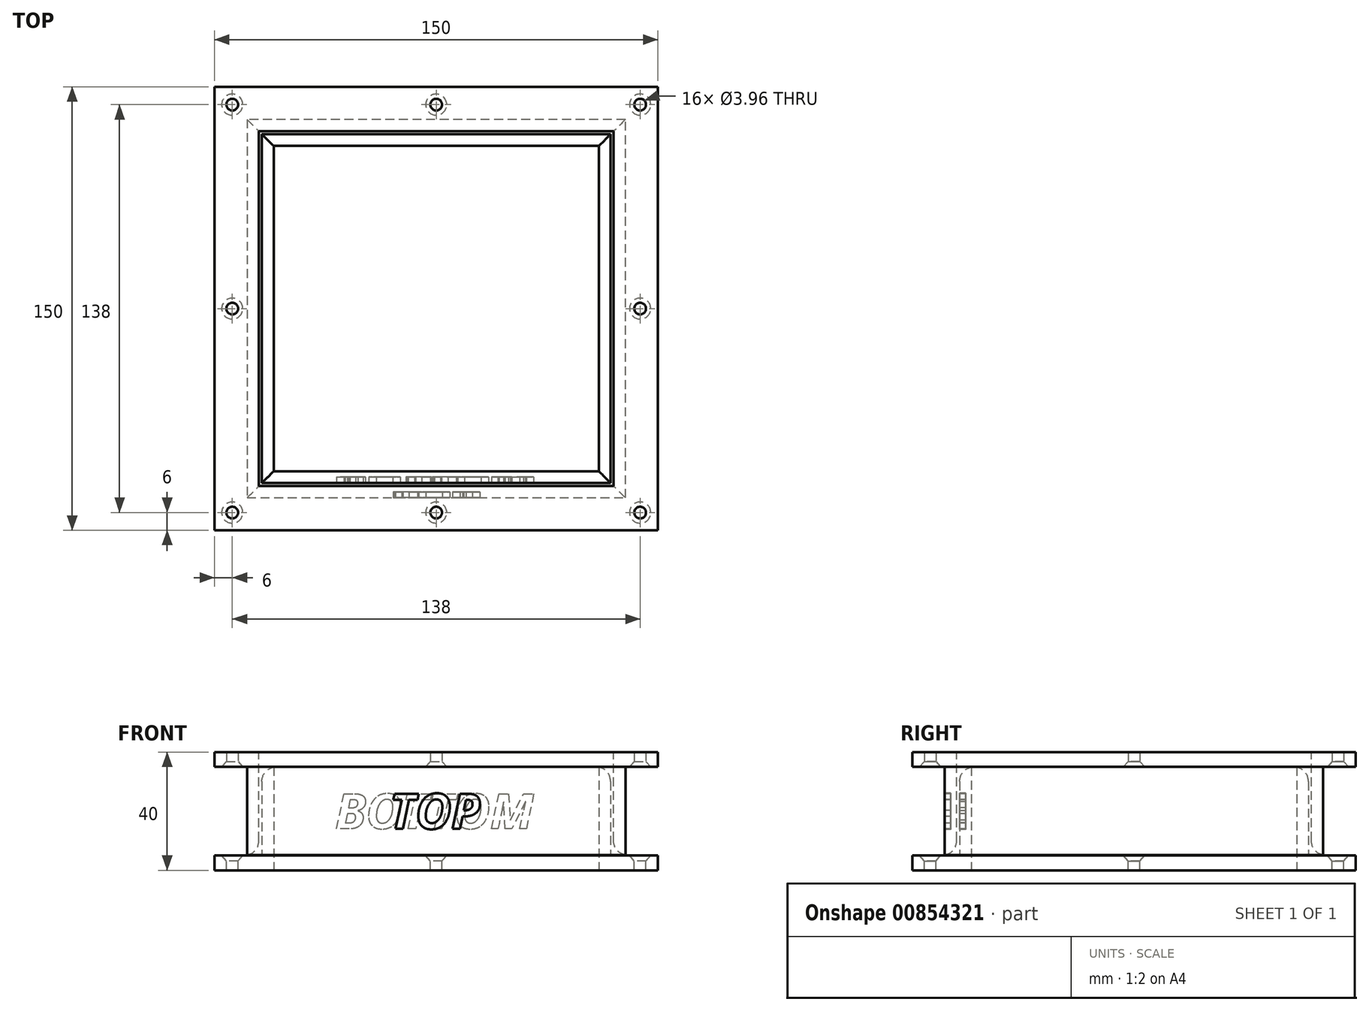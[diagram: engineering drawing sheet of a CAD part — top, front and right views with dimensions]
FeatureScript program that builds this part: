
annotation { "Feature Type Name" : "Feature", "Feature Type Description" : "" }
export const myFeature = defineFeature(function(context is Context, id is Id, definition is map)
    precondition{}
    {
        {
            var Q0;
            Q0=qCreatedBy(makeId("Top.planeOp"),FACE);
            var sketch = newSketch(context, id + "F0", { "sketchPlane" : qUnion([Q0])});
            skLineSegment(sketch, "E0.bottom", {"start": v(-75, 75) * mm, "end": v(75, 75) * mm});
            skLineSegment(sketch, "E0.top", {"start": v(-75, -75) * mm, "end": v(75, -75) * mm});
            skLineSegment(sketch, "E0.left", {"start": v(-75, 75) * mm, "end": v(-75, -75) * mm});
            skLineSegment(sketch, "E0.right", {"start": v(75, 75) * mm, "end": v(75, -75) * mm});
            skLineSegment(sketch, "E1.bottom", {"start": v(-55, 55) * mm, "end": v(55, 55) * mm});
            skLineSegment(sketch, "E1.top", {"start": v(-55, -55) * mm, "end": v(55, -55) * mm});
            skLineSegment(sketch, "E1.left", {"start": v(-55, 55) * mm, "end": v(-55, -55) * mm});
            skLineSegment(sketch, "E1.right", {"start": v(55, 55) * mm, "end": v(55, -55) * mm});
            skLineSegment(sketch, "E2", {"start": v(0, -75) * mm, "end": v(0, 75) * mm, "construction": true});
            skLineSegment(sketch, "E3", {"start": v(-75, 0) * mm, "end": v(75, 0) * mm, "construction": true});
            skSolve(sketch);
        }
        {
            var Q0;
            Q0 = qSketchRegion(id + "F0", true);
            extrude(context, id + "F1", {"entities" : qUnion([Q0]), "depth" : 5 * mm, "offsetDistance" : 25 * mm});
        }
        {
            var Q0;
            Q0=makeQuery(id+"F1.opExtrude","CAP_FACE",FACE,{"disambiguationData":[OSD([sQuery(id+"F0.wireOp",EDGE,"E0.bottom"),sQuery(id+"F0.wireOp",EDGE,"E0.top"),sQuery(id+"F0.wireOp",EDGE,"E0.left"),sQuery(id+"F0.wireOp",EDGE,"E0.right"),sQuery(id+"F0.wireOp",EDGE,"E1.bottom"),sQuery(id+"F0.wireOp",EDGE,"E1.top"),sQuery(id+"F0.wireOp",EDGE,"E1.left"),sQuery(id+"F0.wireOp",EDGE,"E1.right")])],"isStart":false});
            var sketch = newSketch(context, id + "F2", { "sketchPlane" : qUnion([Q0])});
            skLineSegment(sketch, "E4.0", {"start": v(-55, 55) * mm, "end": v(55, 55) * mm});
            skLineSegment(sketch, "E4.1", {"start": v(-55, 55) * mm, "end": v(-55, -55) * mm});
            skLineSegment(sketch, "E5.0", {"start": v(-55, -55) * mm, "end": v(55, -55) * mm});
            skLineSegment(sketch, "E5.1", {"start": v(55, 55) * mm, "end": v(55, -55) * mm});
            skLineSegment(sketch, "E6.bottom", {"start": v(-59, 59) * mm, "end": v(59, 59) * mm});
            skLineSegment(sketch, "E6.top", {"start": v(-59, -59) * mm, "end": v(59, -59) * mm});
            skLineSegment(sketch, "E6.left", {"start": v(-59, 59) * mm, "end": v(-59, -59) * mm});
            skLineSegment(sketch, "E6.right", {"start": v(59, 59) * mm, "end": v(59, -59) * mm});
            skLineSegment(sketch, "E7", {"start": v(0, -48) * mm, "end": v(0, 49.58) * mm, "construction": true});
            skLineSegment(sketch, "E8", {"start": v(-49.37, 0) * mm, "end": v(50.06, 0) * mm, "construction": true});
            skSolve(sketch);
        }
        {
            var Q0;
            Q0 = qSketchRegion(id + "F2", true);
            extrude(context, id + "F3", {"entities" : qUnion([Q0]), "operationType" : NewBodyOperationType.ADD, "depth" : 30 * mm, "offsetDistance" : 25 * mm});
        }
        {
            var Q0;
            Q0=makeQuery(id+"F3.opExtrude","CAP_FACE",FACE,{"disambiguationData":[OSD([sQuery(id+"F2.wireOp",EDGE,"E4.0"),sQuery(id+"F2.wireOp",EDGE,"E4.1"),sQuery(id+"F2.wireOp",EDGE,"E5.0"),sQuery(id+"F2.wireOp",EDGE,"E5.1"),sQuery(id+"F2.wireOp",EDGE,"E6.bottom"),sQuery(id+"F2.wireOp",EDGE,"E6.top"),sQuery(id+"F2.wireOp",EDGE,"E6.left"),sQuery(id+"F2.wireOp",EDGE,"E6.right")])],"isStart":false});
            var sketch = newSketch(context, id + "F4", { "sketchPlane" : qUnion([Q0])});
            skLineSegment(sketch, "E9.0", {"start": v(-59, 59) * mm, "end": v(59, 59) * mm, "construction": true});
            skLineSegment(sketch, "E9.1", {"start": v(-59, 59) * mm, "end": v(-59, -59) * mm, "construction": true});
            skLineSegment(sketch, "E9.2", {"start": v(-59, -59) * mm, "end": v(59, -59) * mm, "construction": true});
            skLineSegment(sketch, "E9.3", {"start": v(59, 59) * mm, "end": v(59, -59) * mm, "construction": true});
            skLineSegment(sketch, "E10.0", {"start": v(-64, 64) * mm, "end": v(64, 64) * mm});
            skLineSegment(sketch, "E10.1", {"start": v(-64, 64) * mm, "end": v(-64, -64) * mm});
            skLineSegment(sketch, "E10.2", {"start": v(-64, -64) * mm, "end": v(64, -64) * mm});
            skLineSegment(sketch, "E10.3", {"start": v(64, 64) * mm, "end": v(64, -64) * mm});
            skLineSegment(sketch, "E11.0", {"start": v(-60, -60) * mm, "end": v(60, -60) * mm});
            skLineSegment(sketch, "E11.1", {"start": v(-60, 60) * mm, "end": v(-60, -60) * mm});
            skLineSegment(sketch, "E11.2", {"start": v(-60, 60) * mm, "end": v(60, 60) * mm});
            skLineSegment(sketch, "E11.3", {"start": v(60, 60) * mm, "end": v(60, -60) * mm});
            skSolve(sketch);
        }
        {
            var Q0;
            Q0 = qSketchRegion(id + "F4", true);
            extrude(context, id + "F5", {"entities" : qUnion([Q0]), "oppositeDirection" : true, "depth" : 30 * mm, "offsetDistance" : 25 * mm});
        }
        {
            var Q0;
            Q0=makeQuery(id+"F5.opExtrude","CAP_FACE",FACE,{"disambiguationData":[OSD([sQuery(id+"F4.wireOp",EDGE,"E9.0"),sQuery(id+"F4.wireOp",EDGE,"E9.1"),sQuery(id+"F4.wireOp",EDGE,"E9.2"),sQuery(id+"F4.wireOp",EDGE,"E9.3"),sQuery(id+"F4.wireOp",EDGE,"E10.0"),sQuery(id+"F4.wireOp",EDGE,"E10.1"),sQuery(id+"F4.wireOp",EDGE,"E10.2"),sQuery(id+"F4.wireOp",EDGE,"E10.3")])],"isStart":true});
            var sketch = newSketch(context, id + "F6", { "sketchPlane" : qUnion([Q0])});
            skLineSegment(sketch, "E12.0", {"start": v(75, 75) * mm, "end": v(75, -75) * mm});
            skLineSegment(sketch, "E12.1", {"start": v(-75, 75) * mm, "end": v(75, 75) * mm});
            skLineSegment(sketch, "E12.2", {"start": v(-75, 75) * mm, "end": v(-75, -75) * mm});
            skLineSegment(sketch, "E12.3", {"start": v(-75, -75) * mm, "end": v(75, -75) * mm});
            skLineSegment(sketch, "E13.0", {"start": v(-60, -60) * mm, "end": v(60, -60) * mm});
            skLineSegment(sketch, "E13.1", {"start": v(-60, 60) * mm, "end": v(-60, -60) * mm});
            skLineSegment(sketch, "E13.2", {"start": v(-60, 60) * mm, "end": v(60, 60) * mm});
            skLineSegment(sketch, "E13.3", {"start": v(60, 60) * mm, "end": v(60, -60) * mm});
            skSolve(sketch);
        }
        {
            var Q0;
            Q0 = qSketchRegion(id + "F6", true);
            extrude(context, id + "F7", {"entities" : qUnion([Q0]), "operationType" : NewBodyOperationType.ADD, "depth" : 5 * mm, "offsetDistance" : 25 * mm});
        }
        {
            var Q0;
            Q0=makeQuery(id+"F1.opExtrude","CAP_FACE",FACE,{"disambiguationData":[OSD([sQuery(id+"F0.wireOp",EDGE,"E0.bottom"),sQuery(id+"F0.wireOp",EDGE,"E0.top"),sQuery(id+"F0.wireOp",EDGE,"E0.left"),sQuery(id+"F0.wireOp",EDGE,"E0.right"),sQuery(id+"F0.wireOp",EDGE,"E1.bottom"),sQuery(id+"F0.wireOp",EDGE,"E1.top"),sQuery(id+"F0.wireOp",EDGE,"E1.left"),sQuery(id+"F0.wireOp",EDGE,"E1.right")])],"isStart":false});
            var sketch = newSketch(context, id + "F8", { "sketchPlane" : qUnion([Q0])});
            skPoint(sketch, "E14", {"position": v(-69, 69) * mm});
            skPoint(sketch, "E15", {"position": v(69, 69) * mm});
            skPoint(sketch, "E16", {"position": v(-69, -69) * mm});
            skPoint(sketch, "E17", {"position": v(69, -69) * mm});
            skPoint(sketch, "E18", {"position": v(0, 69) * mm});
            skPoint(sketch, "E19", {"position": v(-69, 0) * mm});
            skPoint(sketch, "E20", {"position": v(0, -69) * mm});
            skPoint(sketch, "E21", {"position": v(69, 0) * mm});
            skSolve(sketch);
        }
        {
            var Q0;
            Q0=sQuery(id+"F8.wireOp",VERTEX,"E14");
            var Q1;
            Q1=sQuery(id+"F8.wireOp",VERTEX,"E15");
            var Q2;
            Q2=sQuery(id+"F8.wireOp",VERTEX,"E17");
            var Q3;
            Q3=sQuery(id+"F8.wireOp",VERTEX,"E16");
            var Q4;
            Q4=sQuery(id+"F8.wireOp",VERTEX,"E19");
            var Q5;
            Q5=sQuery(id+"F8.wireOp",VERTEX,"E18");
            var Q6;
            Q6=sQuery(id+"F8.wireOp",VERTEX,"E20");
            var Q7;
            Q7=sQuery(id+"F8.wireOp",VERTEX,"E21");
            var Q8;
            Q8=makeQuery(id+"F1.opExtrude","SWEPT_BODY",BODY,{"disambiguationData":[OSD([sQuery(id+"F0.wireOp",EDGE,"E0.bottom"),sQuery(id+"F0.wireOp",EDGE,"E0.top"),sQuery(id+"F0.wireOp",EDGE,"E0.left"),sQuery(id+"F0.wireOp",EDGE,"E0.right"),sQuery(id+"F0.wireOp",EDGE,"E1.bottom"),sQuery(id+"F0.wireOp",EDGE,"E1.top"),sQuery(id+"F0.wireOp",EDGE,"E1.left"),sQuery(id+"F0.wireOp",EDGE,"E1.right")])]});
            hole(context, id + "F9", {"style" : HoleStyle.C_SINK, "endStyle" : HoleEndStyle.THROUGH, "standardTappedOrClearance" : lookupTablePath({ "fit" : "Normal (ASME)", "standard" : "ANSI", "size" : "#5", "type" : "Clearance" }), "standardBlindInLast" : lookupTablePath({ "fit" : "Normal", "standard" : "ANSI", "engagement" : "75%", "pitch" : "40 tpi", "size" : "#5", "type" : "Clearance & tapped" }), "holeDiameter" : 3.96 * mm, "cSinkDiameter" : 7.14 * mm, "cSinkAngle" : 82 * degree, "majorDiameter" : 3.5 * mm, "isTappedThrough" : true, "tappedDepth" : 12 * mm, "tapClearance" : 3, "locations" : qUnion([Q0, Q1, Q2, Q3, Q4, Q5, Q6, Q7]), "scope" : qUnion([Q8])});
        }
        {
            var Q0;
            Q0=makeQuery(id+"F3.opExtrude","SWEPT_FACE",FACE,{"disambiguationData":[OSD([sQuery(id+"F2.wireOp",EDGE,"E6.top")])]});
            var sketch = newSketch(context, id + "F10", { "sketchPlane" : qUnion([Q0])});
            skLineSegment(sketch, "E22", {"start": v(-59, 20) * mm, "end": v(59, 20) * mm, "construction": true});
            skLineSegment(sketch, "E23", {"start": v(0, 35) * mm, "end": v(0, 5) * mm, "construction": true});
            skText(sketch, "E24", { "text": "BOTTOM", "fontName": "OpenSans-BoldItalic.ttf"});
            const initialGuessF10  = {"E24": [-0.0341, 0.014, 1, 0, 0.012]};
            skSetInitialGuess(sketch, initialGuessF10);
            skSolve(sketch);
        }
        {
            var Q0;
            Q0 = qSketchRegion(id + "F10", true);
            extrude(context, id + "F11", {"entities" : qUnion([Q0]), "operationType" : NewBodyOperationType.REMOVE, "oppositeDirection" : true, "depth" : 2 * mm, "offsetDistance" : 25 * mm});
        }
        {
            var Q0;
            Q0=makeQuery(id+"F7.opExtrude","CAP_FACE",FACE,{"disambiguationData":[OSD([sQuery(id+"F6.wireOp",EDGE,"E12.0"),sQuery(id+"F6.wireOp",EDGE,"E12.1"),sQuery(id+"F6.wireOp",EDGE,"E12.2"),sQuery(id+"F6.wireOp",EDGE,"E12.3"),sQuery(id+"F6.wireOp",EDGE,"147194ed-eec6-48fc-bbfb-cd27aaa17bc2.0"),sQuery(id+"F6.wireOp",EDGE,"147194ed-eec6-48fc-bbfb-cd27aaa17bc2.1"),sQuery(id+"F6.wireOp",EDGE,"147194ed-eec6-48fc-bbfb-cd27aaa17bc2.2"),sQuery(id+"F6.wireOp",EDGE,"147194ed-eec6-48fc-bbfb-cd27aaa17bc2.3")])],"isStart":true});
            var sketch = newSketch(context, id + "F12", { "sketchPlane" : qUnion([Q0])});
            skPoint(sketch, "E25", {"position": v(-69, 69) * mm});
            skPoint(sketch, "E26", {"position": v(-69, -69) * mm});
            skPoint(sketch, "E27", {"position": v(69, -69) * mm});
            skPoint(sketch, "E28", {"position": v(69, 69) * mm});
            skPoint(sketch, "E29", {"position": v(0, 69) * mm});
            skPoint(sketch, "E30", {"position": v(-69, 0) * mm});
            skPoint(sketch, "E31", {"position": v(0, -69) * mm});
            skPoint(sketch, "E32", {"position": v(69, 0) * mm});
            skSolve(sketch);
        }
        {
            var Q0;
            Q0=sQuery(id+"F12.wireOp",VERTEX,"E25");
            var Q1;
            Q1=sQuery(id+"F12.wireOp",VERTEX,"E29");
            var Q2;
            Q2=sQuery(id+"F12.wireOp",VERTEX,"E28");
            var Q3;
            Q3=sQuery(id+"F12.wireOp",VERTEX,"E32");
            var Q4;
            Q4=sQuery(id+"F12.wireOp",VERTEX,"E27");
            var Q5;
            Q5=sQuery(id+"F12.wireOp",VERTEX,"E31");
            var Q6;
            Q6=sQuery(id+"F12.wireOp",VERTEX,"E26");
            var Q7;
            Q7=sQuery(id+"F12.wireOp",VERTEX,"E30");
            var Q8;
            Q8=makeQuery(id+"F5.opExtrude","SWEPT_BODY",BODY,{"disambiguationData":[OSD([sQuery(id+"F4.wireOp",EDGE,"E9.0"),sQuery(id+"F4.wireOp",EDGE,"E9.1"),sQuery(id+"F4.wireOp",EDGE,"E9.2"),sQuery(id+"F4.wireOp",EDGE,"E9.3"),sQuery(id+"F4.wireOp",EDGE,"E10.0"),sQuery(id+"F4.wireOp",EDGE,"E10.1"),sQuery(id+"F4.wireOp",EDGE,"E10.2"),sQuery(id+"F4.wireOp",EDGE,"E10.3")])]});
            hole(context, id + "F13", {"style" : HoleStyle.C_SINK, "endStyle" : HoleEndStyle.THROUGH, "standardTappedOrClearance" : lookupTablePath({ "fit" : "Normal (ASME)", "standard" : "ANSI", "size" : "#5", "type" : "Clearance" }), "standardBlindInLast" : lookupTablePath({ "fit" : "Normal", "standard" : "ANSI", "engagement" : "75%", "pitch" : "40 tpi", "size" : "#5", "type" : "Clearance & tapped" }), "holeDiameter" : 3.96 * mm, "cSinkDiameter" : 7.14 * mm, "cSinkAngle" : 82 * degree, "majorDiameter" : 5 * mm, "isTappedThrough" : true, "tappedDepth" : 12 * mm, "tapClearance" : 3, "locations" : qUnion([Q0, Q1, Q2, Q3, Q4, Q5, Q6, Q7]), "scope" : qUnion([Q8])});
        }
        {
            var Q0;
            Q0=makeQuery(id+"F5.opExtrude","SWEPT_FACE",FACE,{"disambiguationData":[OSD([sQuery(id+"F4.wireOp",EDGE,"E10.2")])]});
            var sketch = newSketch(context, id + "F14", { "sketchPlane" : qUnion([Q0])});
            skText(sketch, "E33", { "text": "TOP", "fontName": "OpenSans-BoldItalic.ttf"});
            skLineSegment(sketch, "E34", {"start": v(0, 35) * mm, "end": v(0, 5) * mm, "construction": true});
            skLineSegment(sketch, "E35", {"start": v(64, 20) * mm, "end": v(-64, 20) * mm, "construction": true});
            const initialGuessF14  = {"E33": [-0.01589, 0.014, 1, 0, 0.012]};
            skSetInitialGuess(sketch, initialGuessF14);
            skSolve(sketch);
        }
        {
            var Q0;
            Q0 = qSketchRegion(id + "F14", true);
            extrude(context, id + "F15", {"entities" : qUnion([Q0]), "operationType" : NewBodyOperationType.REMOVE, "oppositeDirection" : true, "depth" : 2 * mm, "offsetDistance" : 25 * mm});
        }
        {
            var Q0;
            Q0=makeQuery(id+"F3.opExtrude","CAP_EDGE",EDGE,{"disambiguationData":[OSD([sQuery(id+"F2.wireOp",EDGE,"E6.top")])],"isStart":false});
            var Q1;
            Q1=makeQuery(id+"F3.opExtrude","CAP_EDGE",EDGE,{"disambiguationData":[OSD([sQuery(id+"F2.wireOp",EDGE,"E6.left")])],"isStart":false});
            var Q2;
            Q2=makeQuery(id+"F3.opExtrude","CAP_EDGE",EDGE,{"disambiguationData":[OSD([sQuery(id+"F2.wireOp",EDGE,"E6.right")])],"isStart":false});
            var Q3;
            Q3=makeQuery(id+"F3.opExtrude","CAP_EDGE",EDGE,{"disambiguationData":[OSD([sQuery(id+"F2.wireOp",EDGE,"E6.bottom")])],"isStart":false});
            fillet(context, id + "F16", {"entities" : qUnion([Q0, Q1, Q2, Q3]), "radius" : 5 * mm, "tangentPropagation" : true, "allowEdgeOverflow" : false});
        }
        {
            var Q0;
            Q0=makeQuery(id+"F5.opExtrude","CAP_EDGE",EDGE,{"disambiguationData":[OSD([sQuery(id+"F4.wireOp",EDGE,"E11.0")])],"isStart":false});
            var Q1;
            Q1=makeQuery(id+"F5.opExtrude","CAP_EDGE",EDGE,{"disambiguationData":[OSD([sQuery(id+"F4.wireOp",EDGE,"E11.1")])],"isStart":false});
            var Q2;
            Q2=makeQuery(id+"F5.opExtrude","CAP_EDGE",EDGE,{"disambiguationData":[OSD([sQuery(id+"F4.wireOp",EDGE,"E11.2")])],"isStart":false});
            var Q3;
            Q3=makeQuery(id+"F5.opExtrude","CAP_EDGE",EDGE,{"disambiguationData":[OSD([sQuery(id+"F4.wireOp",EDGE,"E11.3")])],"isStart":false});
            fillet(context, id + "F17", {"entities" : qUnion([Q0, Q1, Q2, Q3]), "radius" : 5 * mm, "tangentPropagation" : true, "allowEdgeOverflow" : false});
        }
    });
